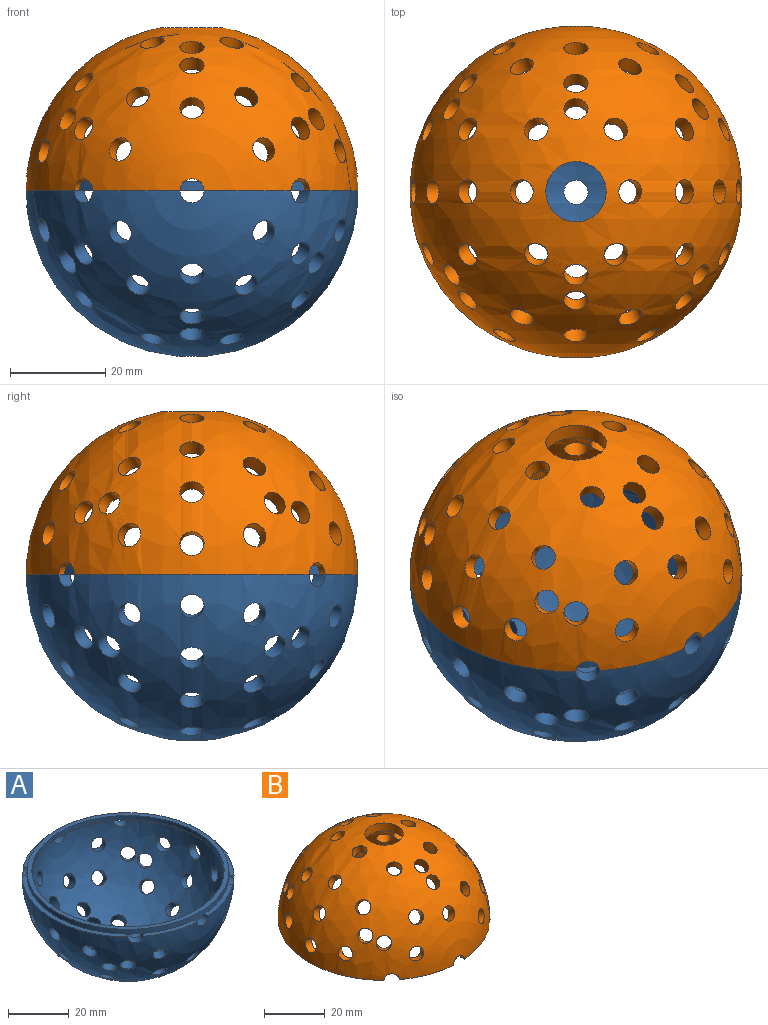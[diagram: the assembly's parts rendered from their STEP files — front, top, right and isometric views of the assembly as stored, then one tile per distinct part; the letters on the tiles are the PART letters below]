
ASSEMBLY  parts=2 mates=1
PART A: 61 faces, bbox 69.9x69.7x36.8 mm
  f0: plane 49.34x11.27mm, normal (0,0,1), area 86.9mm2, adj f49,f54,f55,f57
  f1: plane 18.34x8.07mm, normal (0,0,1), area 31.4mm2, adj f52,f53,f55,f57
  f2: plane 18.34x8.07mm, normal (0,0,1), area 31.4mm2, adj f49,f50,f55,f57
  f3: plane 18.34x8.07mm, normal (0,0,1), area 31.4mm2, adj f50,f51,f55,f57
  f4: plane 49.34x11.27mm, normal (0,0,1), area 86.9mm2, adj f51,f52,f55,f57
  f5: plane 18.34x8.07mm, normal (0,0,1), area 31.4mm2, adj f53,f54,f55,f57
  f6: cylinder r=2.54mm len=5.84mm, axis (0.33,0,0.94), area 50.8mm2, adj f55,f56
  f7: cylinder r=2.54mm len=5.91mm, axis (0.24,0.38,0.89), area 50.8mm2, adj f55,f56
  f8: cylinder r=2.54mm len=5.99mm, axis (-0.33,0.76,0.57), area 50.8mm2, adj f55,f56
  f9: cylinder r=2.54mm len=5.91mm, axis (0.89,-0.38,-0.24), area 50.8mm2, adj f55,f56
  f10: cylinder r=2.54mm len=5.91mm, axis (0.24,-0.38,0.89), area 50.8mm2, adj f55,f56
  f11: cylinder r=2.54mm len=5.91mm, axis (0.89,0.38,-0.24), area 50.8mm2, adj f55,f56
  f12: cylinder r=2.54mm len=5.99mm, axis (0.33,0.76,-0.57), area 50.8mm2, adj f55,f56
  f13: cylinder r=2.54mm len=5.96mm, axis (-0.43,-0.87,-0.25), area 50.8mm2, adj f55,f56
  f14: cylinder r=2.54mm len=5.99mm, axis (-0.75,-0.5,-0.43), area 50.8mm2, adj f55,f56
  f15: cylinder r=2.54mm len=5.99mm, axis (0.75,-0.5,0.43), area 50.8mm2, adj f55,f56
  f16: cylinder r=2.54mm len=5.96mm, axis (0.43,-0.87,0.25), area 50.8mm2, adj f55,f56
  f17: cylinder r=2.54mm len=5.99mm, axis (0.87,0,0.5), area 50.8mm2, adj f55,f56
  f18: cylinder r=2.54mm len=5.84mm, axis (-0.33,0,0.94), area 50.8mm2, adj f55,f56
  f19: cylinder r=2.54mm len=5.92mm, axis (0,0.65,0.76), area 50.8mm2, adj f55,f56
  f20: cylinder r=2.54mm len=5.91mm, axis (-0.24,0.38,0.89), area 50.8mm2, adj f55,f56
  f21: cylinder r=2.54mm len=5.99mm, axis (0.33,0.76,0.57), area 50.8mm2, adj f55,f56
  f22: cylinder r=2.54mm len=5.08mm, axis (0,0,1), area 50.8mm2, adj f55,f56
  f23: cylinder r=2.54mm len=5.92mm, axis (0.65,0,0.76), area 50.8mm2, adj f55,f56
  f24: cylinder r=2.54mm len=5.92mm, axis (-0.65,0.65,0.38), area 50.8mm2, adj f55,f56
  f25: cylinder r=2.54mm len=5.92mm, axis (0.65,0.65,0.38), area 50.8mm2, adj f55,f56
  f26: cylinder r=2.54mm len=5.92mm, axis (-0.65,-0.38,0.65), area 50.8mm2, adj f55,f56
  f27: cylinder r=2.54mm len=5.93mm, axis (0.65,-0.38,0.65), area 50.8mm2, adj f55,f56
  f28: cylinder r=2.54mm len=5.92mm, axis (0.65,0.38,0.65), area 50.8mm2, adj f55,f56
  f29: cylinder r=2.54mm len=5.92mm, axis (-0.65,0.38,0.65), area 50.8mm2, adj f55,f56
  f30: cylinder r=2.54mm len=5.92mm, axis (-0.65,-0.65,0.38), area 50.8mm2, adj f55,f56
  f31: cylinder r=2.54mm len=5.93mm, axis (0.65,-0.65,0.38), area 50.8mm2, adj f55,f56
  f32: cylinder r=2.54mm len=5.92mm, axis (-0.65,0,0.76), area 50.8mm2, adj f55,f56
  f33: cylinder r=2.54mm len=5.99mm, axis (0,-0.87,0.5), area 50.8mm2, adj f55,f56
  f34: cylinder r=2.54mm len=5.99mm, axis (0,-0.5,0.87), area 50.8mm2, adj f55,f56
  f35: cylinder r=2.54mm len=5.99mm, axis (0,-0.5,-0.87), area 50.8mm2, adj f55,f56
  f36: cylinder r=2.54mm len=5.99mm, axis (0,-0.87,-0.5), area 50.8mm2, adj f55,f56
  f37: cylinder r=2.54mm len=5.96mm, axis (0.43,-0.87,-0.25), area 50.8mm2, adj f55,f56
  f38: cylinder r=2.54mm len=5.99mm, axis (0.75,-0.5,-0.43), area 50.8mm2, adj f55,f56
  f39: cylinder r=2.54mm len=5.99mm, axis (-0.75,-0.5,0.43), area 50.8mm2, adj f55,f56
  f40: cylinder r=2.54mm len=5.96mm, axis (-0.43,-0.87,0.25), area 50.8mm2, adj f55,f56
  f41: cylinder r=2.54mm len=5.99mm, axis (-0.87,0,0.5), area 50.8mm2, adj f55,f56
  f42: cylinder r=2.54mm len=5.91mm, axis (-0.89,-0.38,-0.24), area 50.8mm2, adj f55,f56
  f43: cylinder r=2.54mm len=5.59mm, axis (-0.98,0,-0.19), area 50.8mm2, adj f55,f56
  f44: cylinder r=2.54mm len=5.92mm, axis (0,-0.65,0.76), area 50.8mm2, adj f55,f56
  f45: cylinder r=2.54mm len=5.91mm, axis (-0.24,-0.38,0.89), area 50.8mm2, adj f55,f56
  f46: cylinder r=2.54mm len=5.91mm, axis (-0.89,0.38,-0.24), area 50.8mm2, adj f55,f56
  f47: cylinder r=2.54mm len=5.99mm, axis (-0.33,0.76,-0.57), area 50.8mm2, adj f55,f56
  f48: cylinder r=2.54mm len=5.59mm, axis (0.98,0,-0.19), area 50.8mm2, adj f55,f56
  f49: cylinder r=2.54mm len=5.92mm, axis (0.65,0.76,0), area 25.4mm2, adj f0,f2,f55,f56,f60
  f50: cylinder r=2.54mm len=5.08mm, axis (0,-1,0), area 25.4mm2, adj f2,f3,f55,f56,f60
  f51: cylinder r=2.54mm len=5.92mm, axis (-0.65,0.76,0), area 25.4mm2, adj f3,f4,f55,f56,f60
  f52: cylinder r=2.54mm len=5.92mm, axis (0.65,0.76,0), area 25.4mm2, adj f1,f4,f55,f56,f60
  f53: cylinder r=2.54mm len=5.08mm, axis (0,-1,0), area 25.4mm2, adj f1,f5,f55,f56,f60
  f54: cylinder r=2.54mm len=5.92mm, axis (-0.65,0.76,0), area 25.4mm2, adj f0,f5,f55,f56,f60
  f55: sphere r=34.92mm, area 6730mm2, adj f0,f1,f2,f3,f4,f5,f6,f7
  f56: sphere r=31.75mm, area 5400.4mm2, adj f6,f7,f8,f9,f10,f11,f12,f13
  f57: cylinder r=33.3mm len=66.59mm, axis (0,0,-1), area 398.5mm2, adj f0,f1,f2,f3,f4,f5,f59,f60
  f58: cylinder r=31.7mm len=63.4mm, axis (0,0,-1), area 379.4mm2, adj f59,f60
  f59: plane 66.59x66.59mm, normal (0,0,1), area 326.6mm2, adj f57,f58
  f60: plane 66.59x63.5mm, normal (0,0,-1), area 57.7mm2, adj f49,f50,f51,f52,f53,f54,f56,f57
PART B: 69 faces, bbox 69.9x69.7x34.9 mm
  f0: sphere r=31.75mm, area 4964.7mm2, adj f8,f9,f10,f11,f12,f13,f14,f15
  f1: plane 18.34x8.04mm, normal (0,0,-1), area 30.6mm2, adj f7,f12,f24,f60
  f2: plane 18.34x8.04mm, normal (0,0,-1), area 30.6mm2, adj f7,f15,f24,f58
  f3: plane 18.34x8.04mm, normal (0,0,-1), area 30.6mm2, adj f7,f14,f23,f64
  f4: plane 18.34x8.04mm, normal (0,0,-1), area 30.6mm2, adj f7,f13,f23,f62
  f5: plane 49.34x11.25mm, normal (0,0,-1), area 84.8mm2, adj f7,f13,f15,f66
  f6: plane 49.34x11.25mm, normal (0,0,-1), area 84.8mm2, adj f7,f12,f14,f68
  f7: sphere r=34.92mm, area 6622.7mm2, adj f1,f2,f3,f4,f5,f6,f8,f9
  f8: cylinder r=2.54mm len=5.92mm, axis (0.65,0.38,0.65), area 50.8mm2, adj f0,f7
  f9: cylinder r=2.54mm len=5.93mm, axis (0.65,-0.38,0.65), area 50.8mm2, adj f0,f7
  f10: cylinder r=2.54mm len=5.92mm, axis (-0.65,-0.38,0.65), area 50.8mm2, adj f0,f7
  f11: cylinder r=2.54mm len=5.92mm, axis (-0.65,0.38,0.65), area 50.8mm2, adj f0,f7
  f12: cylinder r=2.54mm len=5.92mm, axis (-0.65,0.76,0), area 18.4mm2, adj f0,f1,f6,f7,f59,f60,f67,f68
  f13: cylinder r=2.54mm len=5.92mm, axis (-0.65,0.76,0), area 18.4mm2, adj f0,f4,f5,f7,f61,f62,f65,f66
  f14: cylinder r=2.54mm len=5.92mm, axis (0.65,0.76,0), area 18.4mm2, adj f0,f3,f6,f7,f63,f64,f67,f68
  f15: cylinder r=2.54mm len=5.92mm, axis (0.65,0.76,0), area 18.4mm2, adj f0,f2,f5,f7,f57,f58,f65,f66
  f16: cylinder r=2.54mm len=5.92mm, axis (0.65,0.65,0.38), area 50.8mm2, adj f0,f7
  f17: cylinder r=2.54mm len=5.92mm, axis (-0.65,0.65,0.38), area 50.8mm2, adj f0,f7
  f18: cylinder r=2.54mm len=5.92mm, axis (-0.65,-0.65,0.38), area 50.8mm2, adj f0,f7
  f19: cylinder r=2.54mm len=5.93mm, axis (0.65,-0.65,0.38), area 50.8mm2, adj f0,f7
  f20: cylinder r=2.54mm len=5.92mm, axis (0.65,0,0.76), area 50.8mm2, adj f0,f7
  f21: cylinder r=2.54mm len=5.92mm, axis (-0.65,0,0.76), area 50.8mm2, adj f0,f7
  f22: cylinder r=2.54mm len=5.99mm, axis (0,-0.87,0.5), area 50.8mm2, adj f0,f7
  f23: cylinder r=2.54mm len=5.08mm, axis (0,-1,0), area 18.4mm2, adj f0,f3,f4,f7,f61,f62,f63,f64
  f24: cylinder r=2.54mm len=5.08mm, axis (0,-1,0), area 18.4mm2, adj f0,f1,f2,f7,f57,f58,f59,f60
  f25: cylinder r=2.54mm len=5.99mm, axis (0,-0.5,0.87), area 50.8mm2, adj f0,f7
  f26: cylinder r=2.54mm len=5.99mm, axis (0,-0.5,-0.87), area 50.8mm2, adj f0,f7
  f27: cylinder r=2.54mm len=5.99mm, axis (0,-0.87,-0.5), area 50.8mm2, adj f0,f7
  f28: cylinder r=2.54mm len=5.96mm, axis (0.43,-0.87,-0.25), area 50.8mm2, adj f0,f7
  f29: cylinder r=2.54mm len=5.99mm, axis (0.75,-0.5,-0.43), area 50.8mm2, adj f0,f7
  f30: cylinder r=2.54mm len=5.99mm, axis (-0.75,-0.5,0.43), area 50.8mm2, adj f0,f7
  f31: cylinder r=2.54mm len=5.96mm, axis (-0.43,-0.87,0.25), area 50.8mm2, adj f0,f7
  f32: cylinder r=2.54mm len=5.99mm, axis (-0.87,0,0.5), area 50.8mm2, adj f0,f7
  f33: cylinder r=2.54mm len=5.92mm, axis (0,0.65,0.76), area 50.8mm2, adj f0,f7
  f34: cylinder r=2.54mm len=5.91mm, axis (-0.89,-0.38,-0.24), area 50.8mm2, adj f0,f7
  f35: cylinder r=2.54mm len=5.91mm, axis (-0.24,0.38,0.89), area 50.8mm2, adj f0,f7
  f36: cylinder r=2.54mm len=5.91mm, axis (-0.89,0.38,-0.24), area 50.8mm2, adj f0,f7
  f37: cylinder r=2.54mm len=5.91mm, axis (-0.24,-0.38,0.89), area 50.8mm2, adj f0,f7
  f38: cylinder r=2.54mm len=5.59mm, axis (-0.98,0,-0.19), area 50.8mm2, adj f0,f7
  f39: cylinder r=2.54mm len=5.92mm, axis (0,-0.65,0.76), area 50.8mm2, adj f0,f7
  f40: cylinder r=2.54mm len=5.99mm, axis (-0.33,0.76,-0.57), area 50.8mm2, adj f0,f7
  f41: cylinder r=2.54mm len=5.99mm, axis (0.33,0.76,0.57), area 50.8mm2, adj f0,f7
  f42: cylinder r=2.54mm len=5.84mm, axis (-0.33,0,0.94), area 50.8mm2, adj f0,f7
  f43: cylinder r=2.54mm len=5.99mm, axis (0.87,0,0.5), area 50.8mm2, adj f0,f7
  f44: cylinder r=2.54mm len=5.96mm, axis (0.43,-0.87,0.25), area 50.8mm2, adj f0,f7
  f45: cylinder r=2.54mm len=5.99mm, axis (0.75,-0.5,0.43), area 50.8mm2, adj f0,f7
  f46: cylinder r=2.54mm len=5.99mm, axis (-0.75,-0.5,-0.43), area 50.8mm2, adj f0,f7
  f47: cylinder r=2.54mm len=5.96mm, axis (-0.43,-0.87,-0.25), area 50.8mm2, adj f0,f7
  f48: cylinder r=2.54mm len=5.99mm, axis (0.33,0.76,-0.57), area 50.8mm2, adj f0,f7
  f49: cylinder r=2.54mm len=5.91mm, axis (0.24,-0.38,0.89), area 50.8mm2, adj f0,f7
  f50: cylinder r=2.54mm len=5.91mm, axis (0.89,0.38,-0.24), area 50.8mm2, adj f0,f7
  f51: cylinder r=2.54mm len=5.59mm, axis (0.98,0,-0.19), area 50.8mm2, adj f0,f7
  f52: cylinder r=2.54mm len=5.91mm, axis (0.89,-0.38,-0.24), area 50.8mm2, adj f0,f7
  f53: cylinder r=2.54mm len=5.91mm, axis (0.24,0.38,0.89), area 50.8mm2, adj f0,f7
  f54: cylinder r=2.54mm len=5.99mm, axis (-0.33,0.76,0.57), area 50.8mm2, adj f0,f7
  f55: cylinder r=2.54mm len=5.84mm, axis (0.33,0,0.94), area 50.8mm2, adj f0,f7
  f56: cylinder r=6.35mm len=12.7mm, axis (0,0,1), area 129mm2, adj f0,f7
  f57: plane 18.85x8.27mm, normal (0,0,-1), area 32.6mm2, adj f0,f15,f24,f58
  f58: cylinder r=33.34mm len=18.85mm, axis (0,0,-1), area 37.3mm2, adj f2,f15,f24,f57
  f59: plane 18.85x8.27mm, normal (0,0,-1), area 32.6mm2, adj f0,f12,f24,f60
  f60: cylinder r=33.34mm len=18.85mm, axis (0,0,-1), area 37.3mm2, adj f1,f12,f24,f59
  f61: plane 18.84x8.27mm, normal (0,0,-1), area 32.6mm2, adj f0,f13,f23,f62
  f62: cylinder r=33.34mm len=18.84mm, axis (0,0,-1), area 37.3mm2, adj f4,f13,f23,f61
  f63: plane 18.84x8.27mm, normal (0,0,-1), area 32.6mm2, adj f0,f14,f23,f64
  f64: cylinder r=33.34mm len=18.84mm, axis (0,0,-1), area 37.3mm2, adj f3,f14,f23,f63
  f65: plane 48.14x11.35mm, normal (0,0,-1), area 86.1mm2, adj f0,f13,f15,f66
  f66: cylinder r=33.34mm len=48.14mm, axis (0,0,-1), area 100.8mm2, adj f5,f13,f15,f65
  f67: plane 48.14x11.35mm, normal (0,0,-1), area 86.1mm2, adj f0,f12,f14,f68
  f68: cylinder r=33.34mm len=48.14mm, axis (0,0,-1), area 100.8mm2, adj f6,f12,f14,f67
PLACE A t=(-30.61,11.99,27.08)mm
PLACE B t=(-111.89,11.99,27.08)mm
MATE fastened A.f22 <-> B.f56  axis (0,0,1) through (-30.61,11.99,27.08)mm
